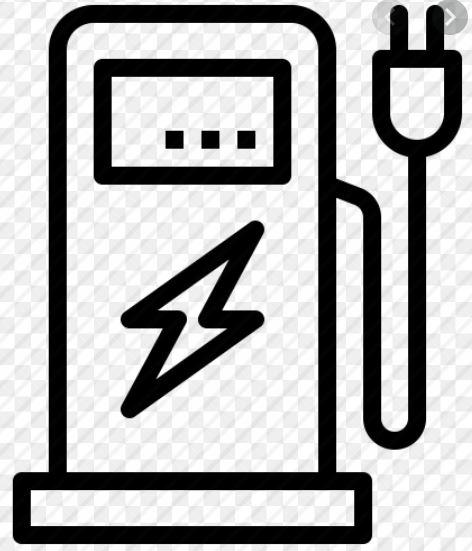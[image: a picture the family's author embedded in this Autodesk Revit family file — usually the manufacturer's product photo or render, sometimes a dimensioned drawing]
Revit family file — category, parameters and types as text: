
# Revit family: Building-ElectricalVehicleCharging-GEWISS-JOINON-ICON_PREMIUM-CABLE
name_source: partatom
category: Apparecchi elettrici
units: mm (PartAtom-declared; Revit-internal decimal feet)

## family parameters
Condiviso = No
Host = Superficie
Mantenere orientamento annotazione = Sì
Punto di calcolo locali = Sì
Quota connettore circolare = Usa diametro
Taglio con vuoti quando caricato = No
Tipo di parte = Normale

## types (12) — shared parameters
(Auto)restart electrical protections = Currently not present
BLOCCO = B=C
Colour = Dark grey
Customizations: = No
DC Leakage check = Yes
External treatments = No
FORMULA = 1000 mm  [stored 3.28084 ft]
Human Interface = LED RGB + slide touch display
IDF = 960366bd-5895-4a82-90a2-4f3db79b1928
INPUT: = -
IP degree = IP55
Immagine tipo = ICON_PREMIUM_S.jpg
L = 155 mm  [stored 0.50853 ft]
Material = Thermoplastic (Post-industrial origin)
Mechanical characteristics = -
Mouting and installation = Wall mounting (floor mounting with support)
N. of sockets Type 2 = 1
N.poli = 1
OUTPUT : = -
Operating temperature: = -25 +50 °C
POMELLO = bianco
PRESA = Giallo
Produttore = GEWISS S.p.A.
Prospetto di default = 1219 mm
Protection : = DC Leak 6mA
STRUTTURA = RAL - 7035
STRUTTURA ALTA = blue
Shock resistance = IK10
Socket/Connector Nr. (Type) = 1 (Type 2 connector with 5 mt. cable)
Spostamento_S = 1500 mm  [stored 4.92126 ft]
Thermal-magnetic protection = Currently not present
Type of Socket = Type 2 mobile with cable
Type of residual current protection = Currently not present
URL = https://www.gewiss.com
VETRO = Vetro
Version file RFA = 19.4
Voltaggio = 0 V
W = 115 mm  [stored 0.377297 ft]

## per-type parameters (varying)
| type | AMBILIGHT | Charging activation | Charging power | Connectivity: | Current supplied (max): | Descrizione | Energy meter | Max power | Modello | Power meter | RFID | Rated current: | Rated insulation voltage (Ui) | Rated voltage | Terminal blocks: | Total power: |
| GWJ3313A - WB ICON PREM.A. AUT.DLM 11 kW T2C IP55 | Yes | Free access, with dynamic load management | 11 kW | BLE | 16 Ampere | WB ICON PREM.A. AUT.DLM 11 kW T2C IP55 |  | 11 Chilowatt | GWJ3313A | Currently not present |  | 16 Ampere | 400 Volt | 400 Volt | 5 x 10 mm² | 11 Chilowatt |
| GWJ3212L - WB ICON PREM. RFID 7 kW T2C IP55 - ETH |  | Remotely managed, via OCPP 1.6J | 7,4 kW | LAN | 32 Ampere | WB ICON PREM. RFID 7 kW T2C IP55 - ETH | YES (MID) | 7,4 Chilowatt | GWJ3212L | YES (MID) | Yes | 32 Ampere | 230 Volt | 230 Volt | 3 x 10 mm² | 7,4 Chilowatt |
| GWJ3214L - WB ICON PREM. RFID 22 kW T2C IP55 - ETH |  | Remotely managed, via OCPP 1.6J | 22 kW | LAN | 32 Ampere | WB ICON PREM. RFID 22 kW T2C IP55 - ETH | YES (MID) | 22 Chilowatt | GWJ3214L | YES (MID) | Yes | 32 Ampere | 400 Volt | 400 Volt | 5 x 10 mm² | 22 Chilowatt |
| GWJ3214R - WB ICON PREM. RFID 22 kW T2C IP55 |  | Locally managed, via RFID | 22 kW | No | 32 Ampere | WB ICON PREM. RFID 22 kW T2C IP55 | YES (MID) | 22 Chilowatt | GWJ3214R | YES (MID) | Yes | 32 Ampere | 400 Volt | 400 Volt | 5 x 10 mm² | 22 Chilowatt |
| GWJ3212A - WB ICON PREM. AUT.DLM 7 kW T2C IP55 |  | Free access | 7,4 kW | No | 32 Ampere | WB ICON PREM. AUT.DLM 7 kW T2C IP55 |  | 7,4 Chilowatt | GWJ3212A | Currently not present |  | 32 Ampere | 230 Volt | 230 Volt | 3 x 10 mm² | 7,4 Chilowatt |
| GWJ3212W - WB ICON PREM. RFID 7 kW T2C IP55 - 4G |  | Remotely managed, via OCPP 1.6J | 7,4 kW | LAN,4G | 32 Ampere | WB ICON PREM. RFID 7 kW T2C IP55 - 4G | YES (MID) | 7,4 Chilowatt | GWJ3212W | YES (MID) | Yes | 32 Ampere | 230 Volt | 230 Volt | 3 x 10 mm² | 7,4 Chilowatt |
| GWJ3213A - WB ICON PREM. AUT.DLM 11 kW T2C IP55 |  | Free access | 11 kW | No | 16 Ampere | WB ICON PREM. AUT.DLM 11 kW T2C IP55 |  | 11 Chilowatt | GWJ3213A | Currently not present |  | 16 Ampere | 400 Volt | 400 Volt | 5 x 10 mm² | 11 Chilowatt |
| GWJ3211A - WB ICON PREM. AUT. DLM 4 kW T2C IP55 |  | Free access | 4,6 kW | No | 20 Ampere | WB ICON PREM. AUT. DLM 4 kW T2C IP55 |  | 4,6 Chilowatt | GWJ3211A | Currently not present |  | 20 Ampere | 230 Volt | 230 Volt | 3 x 10 mm² | 4,6 Chilowatt |
| GWJ3311A - WB ICON PREM.A. AUT. DLM 4 kW T2C IP55 | Yes | Free access, with dynamic load management | 4,6 kW | BLE | 20 Ampere | WB ICON PREM.A. AUT. DLM 4 kW T2C IP55 |  | 4,6 Chilowatt | GWJ3311A | Currently not present |  | 20 Ampere | 230 Volt | 230 Volt | 3 x 10 mm² | 4,6 Chilowatt |
| GWJ3212R - WB ICON PREM. RFID 7 kW T2C IP55 |  | Locally managed, via RFID | 7,4 kW | No | 32 Ampere | WB ICON PREM. RFID 7 kW T2C IP55 | YES (MID) | 7,4 Chilowatt | GWJ3212R | YES (MID) | Yes | 32 Ampere | 230 Volt | 230 Volt | 3 x 10 mm² | 7,4 Chilowatt |
| GWJ3312A - WB ICON PREM.A. AUT.DLM 7 kW T2C IP55 | Yes | Free access, with dynamic load management | 7,4 kW | BLE | 32 Ampere | WB ICON PREM.A. AUT.DLM 7 kW T2C IP55 |  | 7,4 Chilowatt | GWJ3312A | Currently not present |  | 32 Ampere | 230 Volt | 230 Volt | 3 x 10 mm² | 7,4 Chilowatt |
| GWJ3214W - WB ICON PREM. RFID 22 kW T2C IP55 - 4G |  | Remotely managed, via OCPP 1.6J | 22 kW | LAN,4G | 32 Ampere | WB ICON PREM. RFID 22 kW T2C IP55 - 4G | YES (MID) | 22 Chilowatt | GWJ3214W | YES (MID) | Yes | 32 Ampere | 400 Volt | 400 Volt | 5 x 10 mm² | 22 Chilowatt |

note: [stored X ft] marks values corroborated as IEEE doubles in the binary element streams (Revit-internal decimal feet)

## geometry (parser evidence)
native form markers: Sweep x2
no freeform markers — native parametric forms only
